# Revit family: Trace_cabinet_SC87
name_source: partatom
category: Furniture
revit_build: Autodesk Revit 2017 (Build: 20160225_1515(x64)
units: mm (PartAtom-declared; Revit-internal decimal feet)

## family parameters
Always vertical = Yes
Cut with Voids When Loaded = No
OmniClass Number = 23.40.20.00
OmniClass Title = General Furniture and Specialties
Room Calculation Point = No
Shared = No
Work Plane-Based = No

## types (1)
- Trace_cabinet_SC87
    Depth = 41cm/16,1in
    Design = Space Copenhagen
    Design Year = 2023
    Doors = &tradition Glass Clear
    Height = 190cm/74,8in
    Knobs and Hinges = &tradition Brass brushed
    Manufacturer = &Tradition
    Model = Trace SC87
    Packaging dimensions & weight = Please see product fact sheet available from download page on website
    Type Comments = Trace cabinets
    URL = https://www.andtradition.com
    Variation = Please visit our website to see available colours and finishes.
    Walls and Shelves = &tradition Lacquered Oak
    Width = 50cm/19,7in

## geometry (parser evidence)
native form markers: Sweep x1
no freeform markers — native parametric forms only
